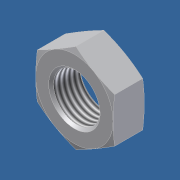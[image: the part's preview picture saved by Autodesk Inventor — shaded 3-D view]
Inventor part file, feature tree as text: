
AUTODESK INVENTOR PART (.ipt)
format: ipt  version: unknown  size: 220,160 bytes
history: native  units: in
note: dims shown in document units (in); Inventor stores cm internally (conversion verified against a paired STEP export)
features: other x70, sketch x3, revolve x2, extrude x1, thread x1
ambient origin geometry x8: Origin, YZ Plane, XZ Plane, XY Plane, X Axis, Y Axis, Z Axis, Center Point
feature tree (77):
  sketch  "Sketch_8"  dims[d0=360.0deg d1=0.38in d2=0.0in]
  sketch  "Sketch_10"  dims[d3=360.0deg d4=0.38in d5=0.0in]
  revolve  "Revolution1"  [1 undecoded]
  extrude  "Extrusion1"  Depth=0.38in TaperAngle=0.0deg
  revolve  "Revolution2"  [1 undecoded]
  thread  "Thread1"  [1 undecoded]
  other  "NUT_XY"
  other  "NUT_YZ"
  other  "NUT_ZX"
  other  "NUT_X"
  other  "NUT_Y"
  other  "NUT_Z"
  other  "NUT_Center"
  other  "a1_XY"
  other  "a1_YZ"
  other  "a1_ZX"
  other  "a1_X"
  other  "a1_Y"
  other  "a1_Z"
  other  "a1_Center"
  other  "a2_XY"
  other  "a2_YZ"
  other  "a2_ZX"
  other  "a2_X"
  other  "a2_Y"
  other  "a2_Z"
  other  "a2_Center"
  other  "b1_XY"
  other  "b1_YZ"
  other  "b1_ZX"
  other  "b1_X"
  other  "b1_Y"
  other  "b1_Z"
  other  "b1_Center"
  other  "b2_XY"
  other  "b2_YZ"
  other  "b2_ZX"
  other  "b2_X"
  other  "b2_Y"
  other  "b2_Z"
  other  "b2_Center"
  other  "e_XY"
  other  "e_YZ"
  other  "e_ZX"
  other  "e_X"
  other  "e_Y"
  other  "e_Z"
  other  "e_Center"
  other  "th1_XY"
  other  "th1_YZ"
  other  "th1_ZX"
  other  "th1_X"
  other  "th1_Y"
  other  "th1_Z"
  other  "th1_Center"
  other  "th2_XY"
  other  "th2_YZ"
  other  "th2_ZX"
  other  "th2_X"
  other  "th2_Y"
  other  "th2_Z"
  other  "th2_Center"
  other  "ol1_XY"
  other  "ol1_YZ"
  other  "ol1_ZX"
  other  "ol1_X"
  other  "ol1_Y"
  other  "ol1_Z"
  other  "ol1_Center"
  other  "ol2_XY"
  other  "ol2_YZ"
  other  "ol2_ZX"
  other  "ol2_X"
  other  "ol2_Y"
  other  "ol2_Z"
  other  "ol2_Center"
  sketch  "Sketch_11"
note: 3 required parameter values undecoded (feature->parameter linkage not recoverable at this tier; creation-order binding heuristic only, values carry confidence <= 0.55)